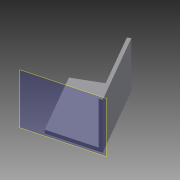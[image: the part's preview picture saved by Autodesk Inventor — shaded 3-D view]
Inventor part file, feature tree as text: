
AUTODESK INVENTOR PART (.ipt)
format: ipt  version: 2015 (Build 190159000, 159)  size: 81,408 bytes
history: native  units: in
note: dims shown in document units (in); Inventor stores cm internally (conversion verified against a paired STEP export)
features: extrude x1, plane x1, split x1, mirror x1, sketch x1
ambient origin geometry x8: Origin, YZ Plane, XZ Plane, XY Plane, X Axis, Y Axis, Z Axis, Center Point
bodies: Solid1 (feature_tree)
feature tree (5):
  extrude  "Extrusion1"  Depth=1.75in
  plane  "Work Plane1"
  split  "Split1"
  mirror  "Mirror1"
  sketch  "Sketch1"  dims[d0=1.75in d1=1.75in d2=0.125in d3=3.0in d4=0.0in d5=15.0deg]
